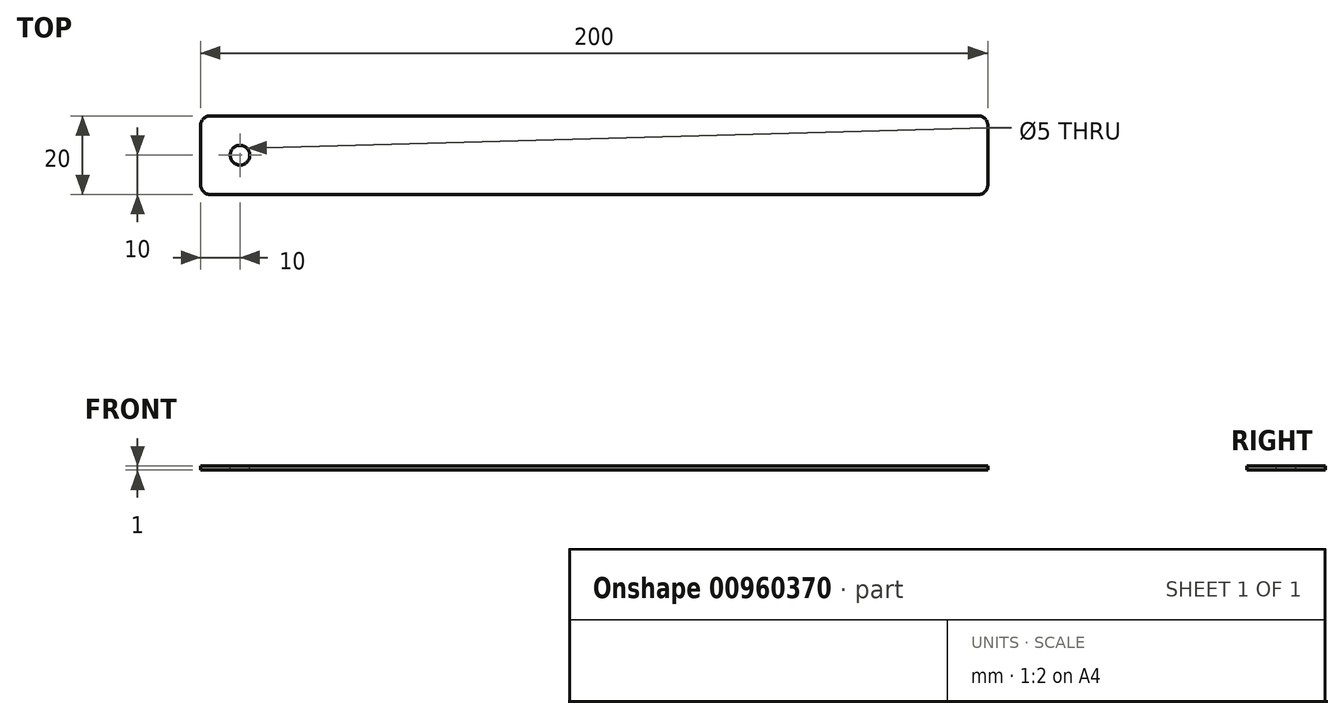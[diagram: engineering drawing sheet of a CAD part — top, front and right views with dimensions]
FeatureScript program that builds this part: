
annotation { "Feature Type Name" : "Feature", "Feature Type Description" : "" }
export const myFeature = defineFeature(function(context is Context, id is Id, definition is map)
    precondition{}
    {
        {
            var Q0;
            Q0=qCreatedBy(makeId("Top.planeOp"),FACE);
            var sketch = newSketch(context, id + "F0", { "sketchPlane" : qUnion([Q0])});
            skLineSegment(sketch, "E0.bottom", {"start": v(0, 0) * mm, "end": v(200, 0) * mm});
            skLineSegment(sketch, "E0.top", {"start": v(0, 20) * mm, "end": v(200, 20) * mm});
            skLineSegment(sketch, "E0.left", {"start": v(0, 0) * mm, "end": v(0, 20) * mm});
            skLineSegment(sketch, "E0.right", {"start": v(200, 0) * mm, "end": v(200, 20) * mm});
            skSolve(sketch);
        }
        {
            var Q0;
            Q0 = qSketchRegion(id + "F0", true);
            extrude(context, id + "F1", {"entities" : qUnion([Q0]), "depth" : 1 * mm, "offsetDistance" : 25 * mm});
        }
        {
            var Q0;
            Q0=makeQuery(id+"F1.opExtrude","CAP_FACE",FACE,{"disambiguationData":[OSD([sQuery(id+"F0.wireOp",EDGE,"E0.bottom"),sQuery(id+"F0.wireOp",EDGE,"E0.top"),sQuery(id+"F0.wireOp",EDGE,"E0.left"),sQuery(id+"F0.wireOp",EDGE,"E0.right")])],"isStart":false});
            var sketch = newSketch(context, id + "F2", { "sketchPlane" : qUnion([Q0])});
            skPoint(sketch, "E1", {"position": v(10, 10) * mm});
            skSolve(sketch);
        }
        {
            var Q0;
            Q0=sQuery(id+"F2.wireOp",VERTEX,"E1");
            var Q1;
            Q1=makeQuery(id+"F1.opExtrude","SWEPT_BODY",BODY,{"disambiguationData":[OSD([sQuery(id+"F0.wireOp",EDGE,"E0.bottom"),sQuery(id+"F0.wireOp",EDGE,"E0.top"),sQuery(id+"F0.wireOp",EDGE,"E0.left"),sQuery(id+"F0.wireOp",EDGE,"E0.right")])]});
            hole(context, id + "F3", {"style" : HoleStyle.SIMPLE, "endStyle" : HoleEndStyle.THROUGH, "holeDiameter" : 5 * mm, "majorDiameter" : 5 * mm, "isTappedThrough" : true, "tappedDepth" : 12 * mm, "tapClearance" : 3, "startFromSketch" : true, "locations" : qUnion([Q0]), "scope" : qUnion([Q1])});
        }
        {
            var Q0;
            Q0=makeQuery(id+"F1.opExtrude","SWEPT_EDGE",EDGE,{"disambiguationData":[OSD([sQuery(id+"F0.wireOp",EDGE,"E0.top"),sQuery(id+"F0.wireOp",EDGE,"E0.left")])]});
            var Q1;
            Q1=makeQuery(id+"F1.opExtrude","SWEPT_EDGE",EDGE,{"disambiguationData":[OSD([sQuery(id+"F0.wireOp",EDGE,"E0.bottom"),sQuery(id+"F0.wireOp",EDGE,"E0.left")])]});
            var Q2;
            Q2=makeQuery(id+"F1.opExtrude","SWEPT_EDGE",EDGE,{"disambiguationData":[OSD([sQuery(id+"F0.wireOp",EDGE,"E0.bottom"),sQuery(id+"F0.wireOp",EDGE,"E0.right")])]});
            var Q3;
            Q3=makeQuery(id+"F1.opExtrude","SWEPT_EDGE",EDGE,{"disambiguationData":[OSD([sQuery(id+"F0.wireOp",EDGE,"E0.top"),sQuery(id+"F0.wireOp",EDGE,"E0.right")])]});
            fillet(context, id + "F4", {"entities" : qUnion([Q0, Q1, Q2, Q3]), "radius" : 2.5 * mm, "tangentPropagation" : true, "allowEdgeOverflow" : false});
        }
    });
